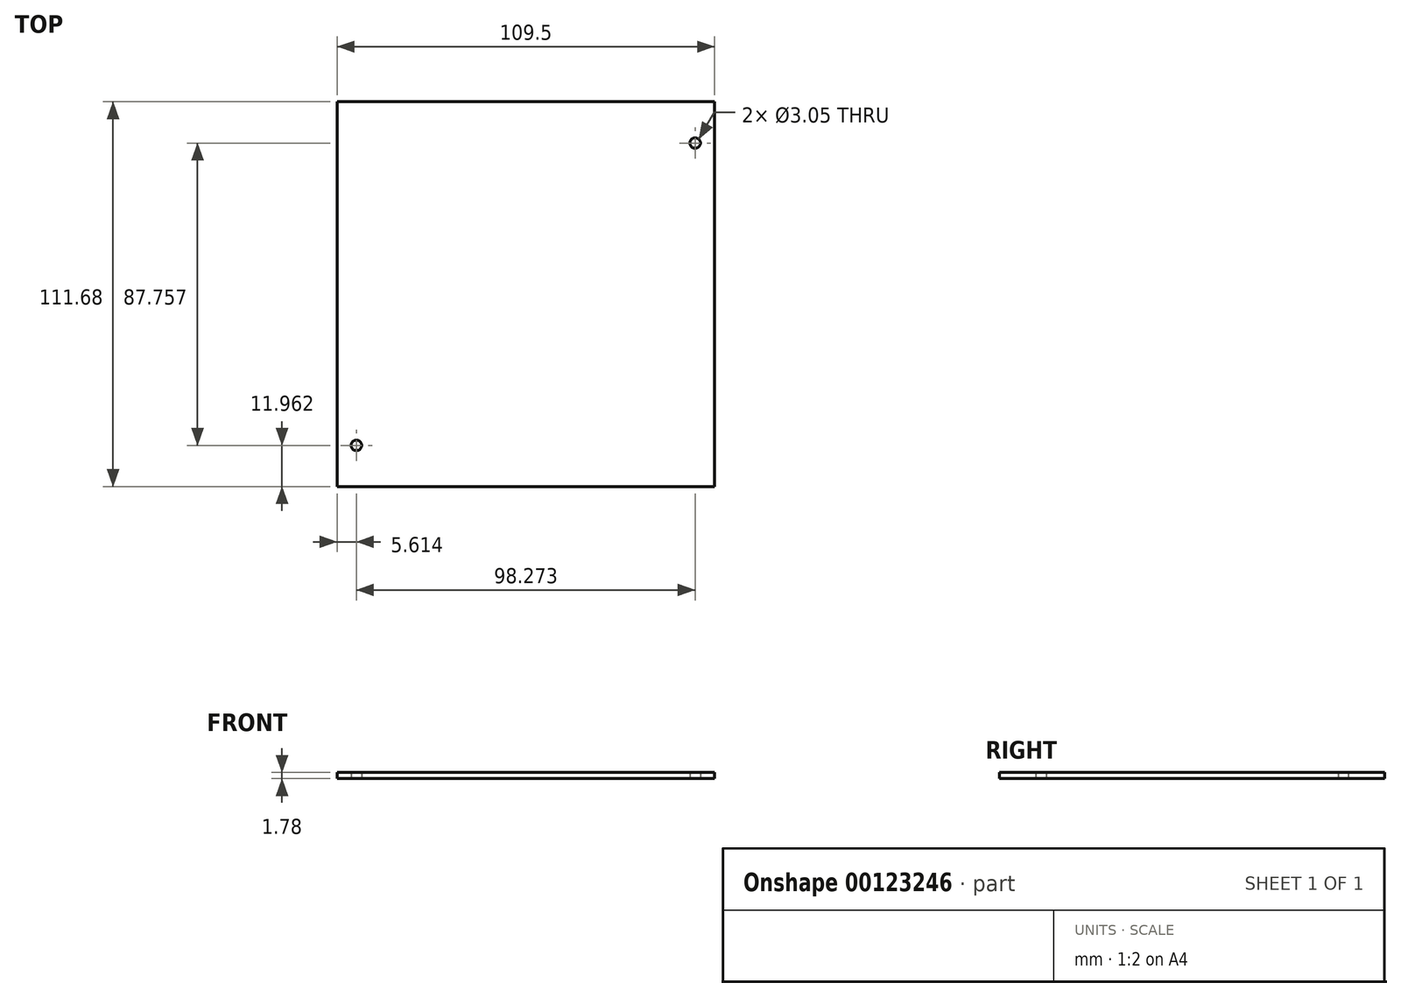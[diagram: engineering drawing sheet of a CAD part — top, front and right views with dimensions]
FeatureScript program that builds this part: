
annotation { "Feature Type Name" : "Feature", "Feature Type Description" : "" }
export const myFeature = defineFeature(function(context is Context, id is Id, definition is map)
    precondition{}
    {
        {
            var Q0;
            Q0=qCreatedBy(makeId("Top.planeOp"),FACE);
            var sketch = newSketch(context, id + "F0", { "sketchPlane" : qUnion([Q0])});
            skLineSegment(sketch, "E0.bottom", {"start": v(-54.75, 55.84) * mm, "end": v(54.75, 55.84) * mm});
            skLineSegment(sketch, "E0.top", {"start": v(-54.75, -55.84) * mm, "end": v(54.75, -55.84) * mm});
            skLineSegment(sketch, "E0.left", {"start": v(-54.75, 55.84) * mm, "end": v(-54.75, -55.84) * mm});
            skLineSegment(sketch, "E0.right", {"start": v(54.75, 55.84) * mm, "end": v(54.75, -55.84) * mm});
            skPoint(sketch, "E0.middle", {"position": v(0, 0) * mm});
            skCircle(sketch, "E1", {"center": v(-49.14, -43.88) * mm, "radius": 1.52 * mm});
            skCircle(sketch, "E2", {"center": v(49.14, 43.88) * mm, "radius": 1.52 * mm});
            skSolve(sketch);
        }
        {
            var Q0;
            Q0 = qSketchRegion(id + "F0", true);
            extrude(context, id + "F1", {"entities" : qUnion([Q0]), "depth" : 1.78 * mm});
        }
    });
